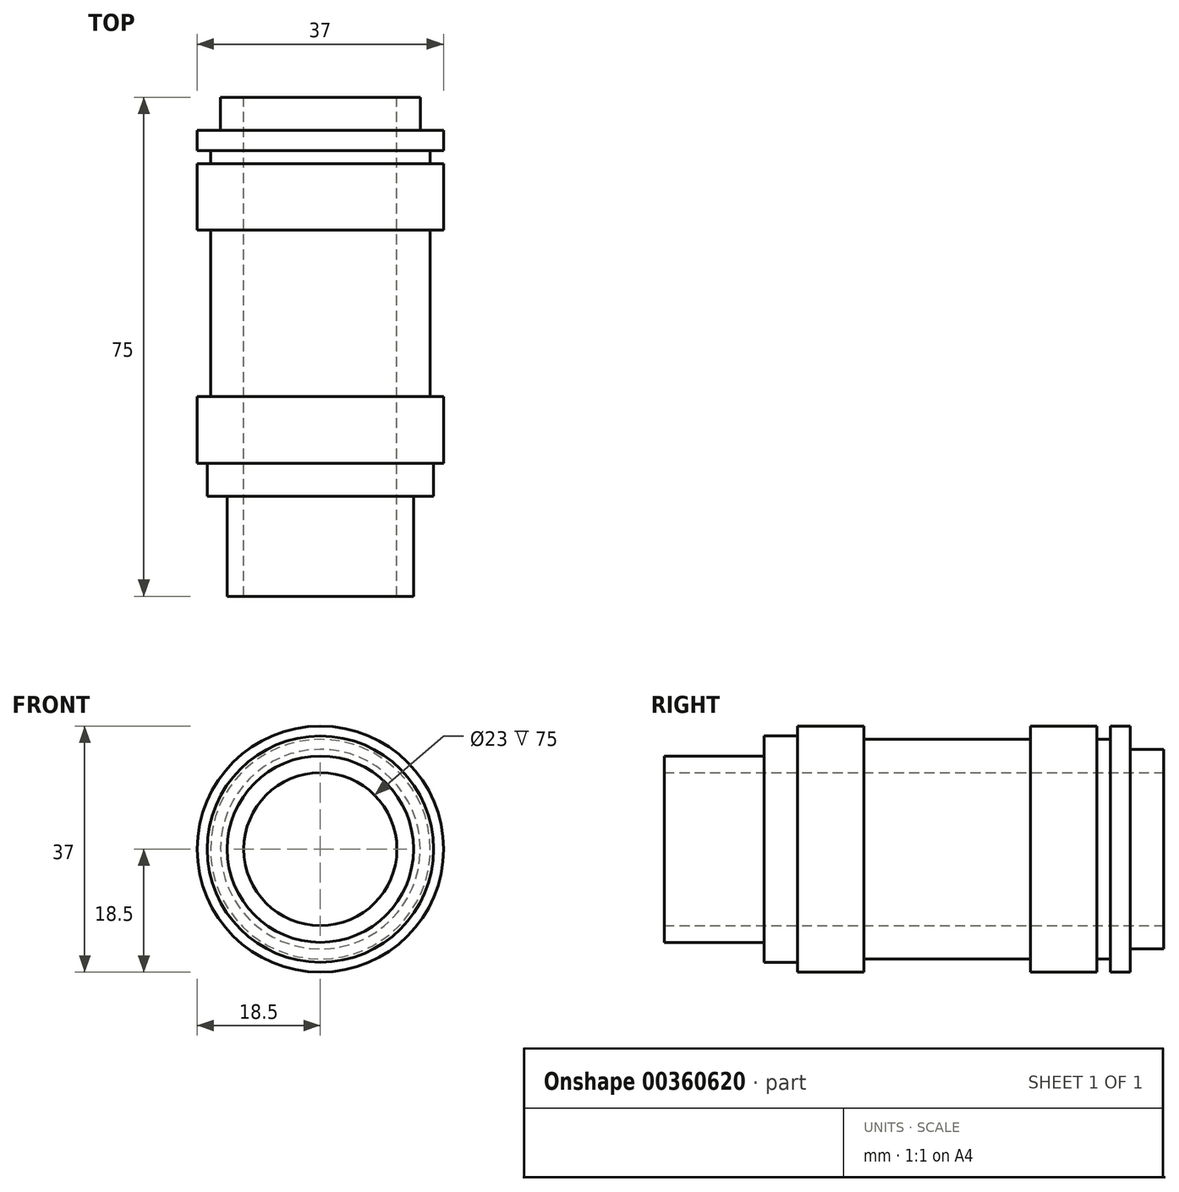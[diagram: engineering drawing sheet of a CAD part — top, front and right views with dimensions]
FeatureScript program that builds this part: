
annotation { "Feature Type Name" : "Feature", "Feature Type Description" : "" }
export const myFeature = defineFeature(function(context is Context, id is Id, definition is map)
    precondition{}
    {
        {
            var Q0;
            Q0=qCreatedBy(makeId("Front.planeOp"),FACE);
            var sketch = newSketch(context, id + "F0", { "sketchPlane" : qUnion([Q0])});
            skCircle(sketch, "E0", {"center": v(0, 0) * mm, "radius": 17 * mm});
            skSolve(sketch);
        }
        {
            var Q0;
            Q0 = qSketchRegion(id + "F0", true);
            extrude(context, id + "F1", {"entities" : qUnion([Q0]), "depth" : 5 * mm});
        }
        {
            var Q0;
            Q0=makeQuery(id+"F1.opExtrude","CAP_FACE",FACE,{"disambiguationData":[OSD([sQuery(id+"F0.wireOp",EDGE,"E0")])],"isStart":false});
            var sketch = newSketch(context, id + "F2", { "sketchPlane" : qUnion([Q0])});
            skCircle(sketch, "E1", {"center": v(0, 0) * mm, "radius": 14 * mm});
            skSolve(sketch);
        }
        {
            var Q0;
            Q0 = qSketchRegion(id + "F2", true);
            extrude(context, id + "F3", {"entities" : qUnion([Q0]), "operationType" : NewBodyOperationType.ADD, "depth" : 15 * mm});
        }
        {
            var Q0;
            Q0=qCreatedBy(makeId("Front.planeOp"),FACE);
            var sketch = newSketch(context, id + "F4", { "sketchPlane" : qUnion([Q0])});
            skCircle(sketch, "E2", {"center": v(0, 0) * mm, "radius": 18.5 * mm});
            skSolve(sketch);
        }
        {
            var Q0;
            Q0 = qSketchRegion(id + "F4", true);
            extrude(context, id + "F5", {"entities" : qUnion([Q0]), "operationType" : NewBodyOperationType.ADD, "oppositeDirection" : true, "depth" : 10 * mm});
        }
        {
            var Q0;
            Q0=qCreatedBy(makeId("Front.planeOp"),FACE);
            var sketch = newSketch(context, id + "F6", { "sketchPlane" : qUnion([Q0])});
            skCircle(sketch, "E3", {"center": v(0, 0) * mm, "radius": 16.5 * mm});
            skSolve(sketch);
        }
        {
            var Q0;
            Q0 = qSketchRegion(id + "F6", true);
            extrude(context, id + "F7", {"entities" : qUnion([Q0]), "operationType" : NewBodyOperationType.ADD, "oppositeDirection" : true, "depth" : 35 * mm});
        }
        {
            var Q0;
            Q0=makeQuery(id+"F7.opExtrude","CAP_FACE",FACE,{"disambiguationData":[OSD([sQuery(id+"F6.wireOp",EDGE,"E3")])],"isStart":false});
            var sketch = newSketch(context, id + "F8", { "sketchPlane" : qUnion([Q0])});
            skCircle(sketch, "E4", {"center": v(0, 0) * mm, "radius": 18.5 * mm});
            skSolve(sketch);
        }
        {
            var Q0;
            Q0 = qSketchRegion(id + "F8", true);
            extrude(context, id + "F9", {"entities" : qUnion([Q0]), "operationType" : NewBodyOperationType.ADD, "depth" : 10 * mm});
        }
        {
            var Q0;
            Q0=makeQuery(id+"F9.opExtrude","CAP_FACE",FACE,{"disambiguationData":[OSD([sQuery(id+"F8.wireOp",EDGE,"E4")])],"isStart":false});
            var sketch = newSketch(context, id + "F10", { "sketchPlane" : qUnion([Q0])});
            skCircle(sketch, "E5", {"center": v(0, 0) * mm, "radius": 16.5 * mm});
            skSolve(sketch);
        }
        {
            var Q0;
            Q0 = qSketchRegion(id + "F10", true);
            extrude(context, id + "F11", {"entities" : qUnion([Q0]), "operationType" : NewBodyOperationType.ADD, "depth" : 2 * mm});
        }
        {
            var Q0;
            Q0=makeQuery(id+"F11.opExtrude","CAP_FACE",FACE,{"disambiguationData":[OSD([sQuery(id+"F10.wireOp",EDGE,"E5")])],"isStart":false});
            var sketch = newSketch(context, id + "F12", { "sketchPlane" : qUnion([Q0])});
            skCircle(sketch, "E6", {"center": v(0, 0) * mm, "radius": 18.5 * mm});
            skSolve(sketch);
        }
        {
            var Q0;
            Q0 = qSketchRegion(id + "F12", true);
            extrude(context, id + "F13", {"entities" : qUnion([Q0]), "operationType" : NewBodyOperationType.ADD, "depth" : 3 * mm});
        }
        {
            var Q0;
            Q0=makeQuery(id+"F13.opExtrude","CAP_FACE",FACE,{"disambiguationData":[OSD([sQuery(id+"F12.wireOp",EDGE,"E6")])],"isStart":false});
            var sketch = newSketch(context, id + "F14", { "sketchPlane" : qUnion([Q0])});
            skCircle(sketch, "E7", {"center": v(0, 0) * mm, "radius": 15 * mm});
            skSolve(sketch);
        }
        {
            var Q0;
            Q0 = qSketchRegion(id + "F14", true);
            extrude(context, id + "F15", {"entities" : qUnion([Q0]), "operationType" : NewBodyOperationType.ADD, "depth" : 5 * mm});
        }
        {
            var Q0;
            Q0=makeQuery(id+"F15.opExtrude","CAP_FACE",FACE,{"disambiguationData":[OSD([sQuery(id+"F14.wireOp",EDGE,"E7")])],"isStart":false});
            var sketch = newSketch(context, id + "F16", { "sketchPlane" : qUnion([Q0])});
            skCircle(sketch, "E8", {"center": v(0, 0) * mm, "radius": 11.5 * mm});
            skSolve(sketch);
        }
        {
            var Q0;
            Q0=makeQuery(id+"F16.imprint","IMPRINT",FACE,{"disambiguationData":[TD([[makeQuery(id+"F16.imprint","IMPRINT",EDGE,{"derivedFrom":sQuery(id+"F16.wireOp",EDGE,"E8")}),1.0]])]});
            extrude(context, id + "F17", {"entities" : qUnion([Q0]), "operationType" : NewBodyOperationType.REMOVE, "oppositeDirection" : true, "depth" : 136.4 * mm});
        }
    });
